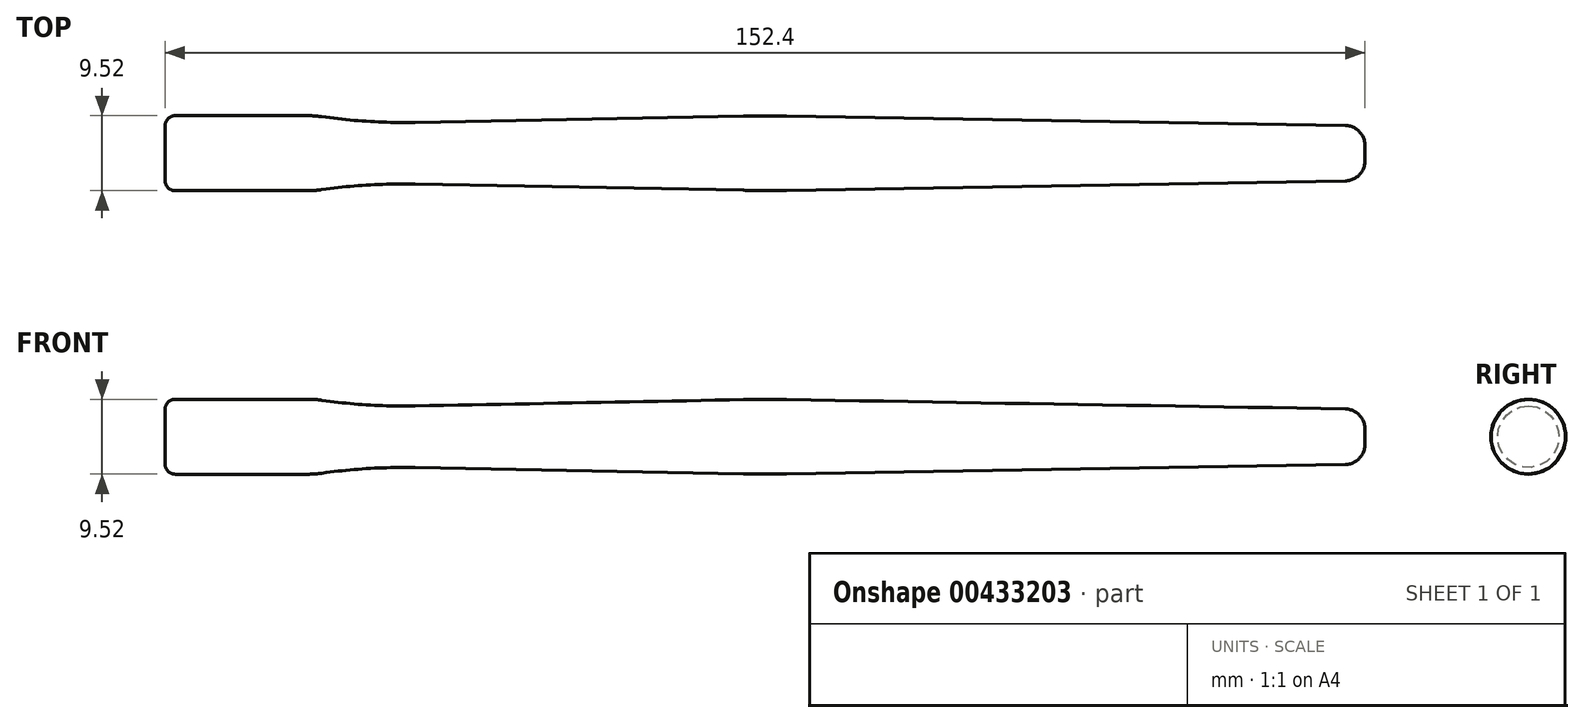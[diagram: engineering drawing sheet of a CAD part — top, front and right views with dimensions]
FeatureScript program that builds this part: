
annotation { "Feature Type Name" : "Feature", "Feature Type Description" : "" }
export const myFeature = defineFeature(function(context is Context, id is Id, definition is map)
    precondition{}
    {
        {
            var Q0;
            Q0=qCreatedBy(makeId("Top.planeOp"),FACE);
            var sketch = newSketch(context, id + "F0", { "sketchPlane" : qUnion([Q0])});
            skLineSegment(sketch, "E0.bottom", {"start": v(-76.2, 4.76) * mm, "end": v(-58.08, 4.76) * mm});
            skLineSegment(sketch, "E0.top", {"start": v(-76.2, -4.76) * mm, "end": v(76.2, -4.76) * mm, "construction": true});
            skLineSegment(sketch, "E0.left", {"start": v(-76.2, 4.76) * mm, "end": v(-76.2, 0) * mm});
            skLineSegment(sketch, "E0.right", {"start": v(76.2, 3.5) * mm, "end": v(76.2, 0) * mm});
            skPoint(sketch, "E0.middle", {"position": v(0, 0) * mm});
            skLineSegment(sketch, "E1", {"start": v(0, 0) * mm, "end": v(0, 4.76) * mm, "construction": true});
            skLineSegment(sketch, "E2", {"start": v(-2.72, 4.71) * mm, "end": v(-44.45, 3.92) * mm});
            skLineSegment(sketch, "E3", {"start": v(-44.45, 3.92) * mm, "end": v(-44.45, -4.76) * mm, "construction": true});
            skPoint(sketch, "E4.end.orphan", {"position": v(-57.15, 3.67) * mm});
            skArc(sketch, "E5", {"start": v(-44.45, 3.92) * mm, "mid": v(-50.39, 4.04) * mm, "end": v(-56.3, 4.64) * mm});
            skPoint(sketch, "E6.visualSharp", {"position": v(-57.15, 4.76) * mm});
            skArc(sketch, "E6.filletArc", {"start": v(-56.3, 4.64) * mm, "mid": v(-57.19, 4.73) * mm, "end": v(-58.08, 4.76) * mm});
            skLineSegment(sketch, "E7", {"start": v(2.72, 4.72) * mm, "end": v(76.2, 3.5) * mm});
            skLineSegment(sketch, "E8", {"start": v(-76.2, 0) * mm, "end": v(76.2, 0) * mm});
            skPoint(sketch, "E9.orphan", {"position": v(76.2, 4.76) * mm});
            skPoint(sketch, "E10.visualSharp", {"position": v(0, 4.76) * mm});
            skArc(sketch, "E10.filletArc", {"start": v(2.72, 4.72) * mm, "mid": v(0, 4.74) * mm, "end": v(-2.72, 4.71) * mm});
            skSolve(sketch);
        }
        {
            var Q0;
            Q0 = qSketchRegion(id + "F0", true);
            var Q1;
            Q1=sQuery(id+"F0.wireOp",EDGE,"E8");
            revolve(context, id + "F1", {"entities" : qUnion([Q0]), "axis" : qUnion([Q1]), "revolveType" : RevolveType.FULL});
        }
        {
            var Q0;
            Q0=makeQuery(id+"F1.opRevolve","SWEPT_EDGE",EDGE,{"disambiguationData":[OSD([sQuery(id+"F0.wireOp",EDGE,"E0.right"),sQuery(id+"F0.wireOp",EDGE,"E7")])]});
            fillet(context, id + "F2", {"entities" : qUnion([Q0]), "radius" : 2.54 * mm, "tangentPropagation" : true, "allowEdgeOverflow" : false});
        }
        {
            var Q0;
            Q0=makeQuery(id+"F1.opRevolve","SWEPT_EDGE",EDGE,{"disambiguationData":[OSD([sQuery(id+"F0.wireOp",EDGE,"E0.bottom"),sQuery(id+"F0.wireOp",EDGE,"E0.left")])]});
            fillet(context, id + "F3", {"entities" : qUnion([Q0]), "radius" : 1.27 * mm, "tangentPropagation" : true, "allowEdgeOverflow" : false});
        }
    });
